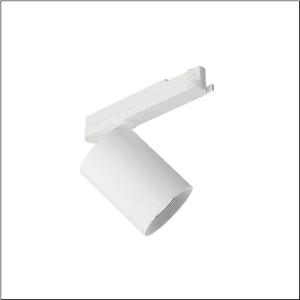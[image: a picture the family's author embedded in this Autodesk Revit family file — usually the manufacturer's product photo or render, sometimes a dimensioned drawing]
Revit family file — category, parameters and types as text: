
# Revit family: spot_21_51se14mbd5b
name_source: partatom
category: Lighting Fixtures
units: mm (PartAtom-declared; Revit-internal decimal feet)

## family parameters
Cut with Voids When Loaded = No
Host = Face
Light Source = No
Part Type = Normal
Room Calculation Point = No
Round Connector Dimension = Use Diameter
Shared = No

## types (1)
- --- (1 x LED, 5490 lm, 41.5 W, 4000K)
    Apparent Load = 42 VA
    CIE Flux Codes = 96 99 100 100 100
    Color Rendering = 90
    Color Temperature = 4000K
    Default Elevation = 1800 mm
    Description = Spot 21, directional spotlight, light control with lens, of PMMA, LED rated luminous flux: 5.270lm, light colour: 940, control gear: ECG Multilumen, with 3-phase adapter, mains connection: 220..240V, AC, 50/60Hz, of aluminium, traffic white (RAL 9016), length: 213mm, diameter: 105mm, protection rating (complete): IP20, insulation class (complete): insulation class I (protective earthing), certification: CE, impact resistance: IK02, permissible ambient temperature for indoor applications: -20..+40°C, packaging unit: 1 piece
    Height = 175 mm
    Lamp = 1 x LED
    Lamp Light Flux = 5490 lm
    Lamp Power = 41.5 W
    Lamp count = 1
    Length = 105 mm
    Luminous efficacy = 132 lm/W
    Manufacturer = Siteco
    ModVariant = No
    Model = 51SE14MBD5B
    Mounting Place = Ceiling
    Mounting Type = Pendant
    Number of Poles = 1
    OnlyDefault = Yes
    Power Factor = 1
    Product Name = Spot 21
    Product group = directional spotlight
    ProductGroupID = 905
    Protection Class = Protection class I
    Protection Degree = IP 20
    RLX_Detail_Level = 1
    RLX_Emergency_Light_Flux = 0 lm
    RLX_Emergency_Type = 0
    RLX_Emergency_Type_DB = No
    RlxData = <blob elided: 17617 chars, md5=510e5d53>
    Socket = socket
    Standby Power = 0 W
    System Light Flux = 5490 lm
    System Power = 42 W
    Type Comments = factory setting: luminous flux: 100 % | (ON | ON | ON | ON) | 1050 mA
    Type Image = l_1003976.jpg
    URL = http://relux.com
    VarID = @adj_075157
    Voltage = 0 V
    Weight = 0.00 kg
    Width = 0 mm  [stored 0 ft]

note: [stored X ft] marks values corroborated as IEEE doubles in the binary element streams (Revit-internal decimal feet)

## geometry (parser evidence)
native form markers: Blend x4, Sweep x8
no freeform markers — native parametric forms only
